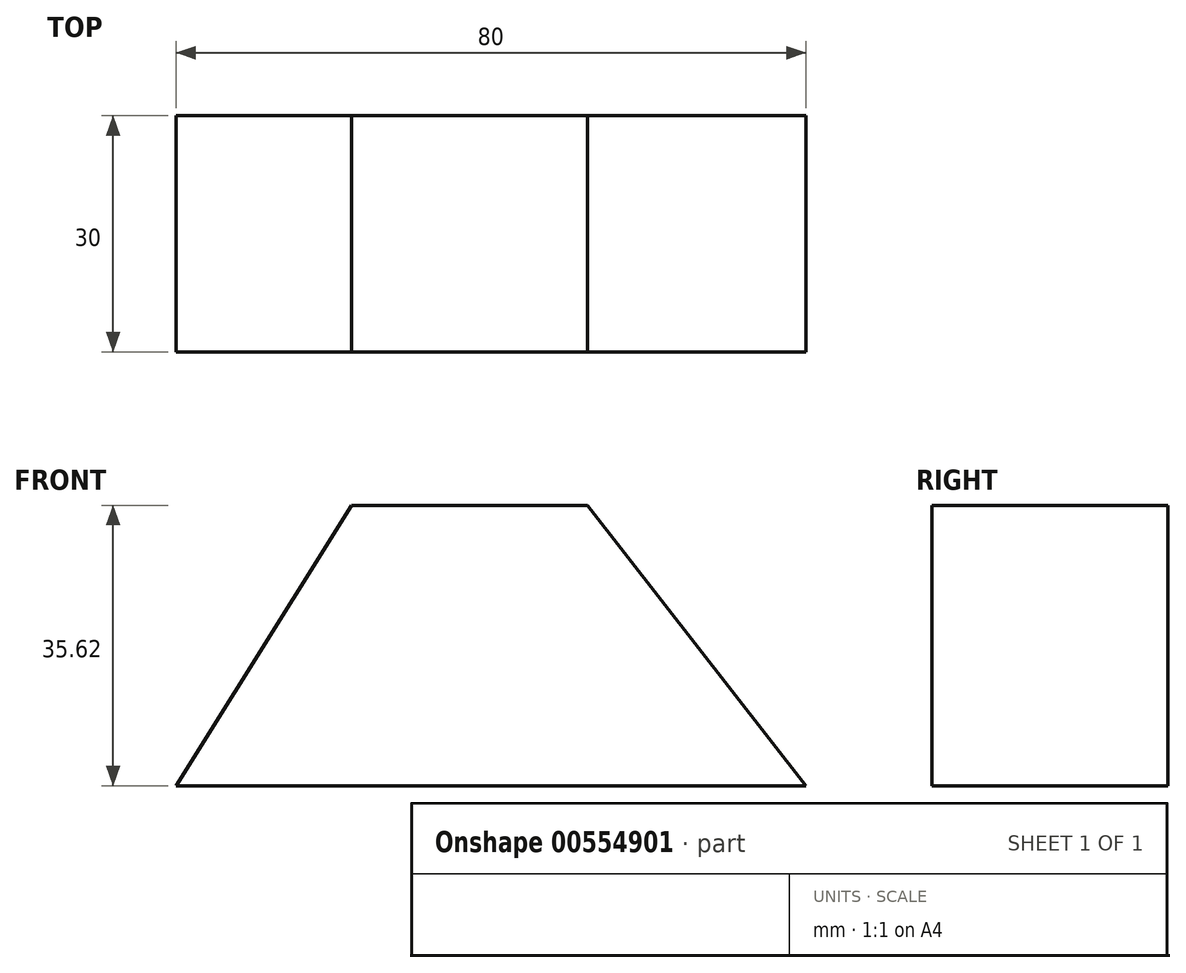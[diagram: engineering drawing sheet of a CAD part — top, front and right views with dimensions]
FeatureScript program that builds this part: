
annotation { "Feature Type Name" : "Feature", "Feature Type Description" : "" }
export const myFeature = defineFeature(function(context is Context, id is Id, definition is map)
    precondition{}
    {
        {
            var Q0;
            Q0=qCreatedBy(makeId("Front.planeOp"),FACE);
            var sketch = newSketch(context, id + "F0", { "sketchPlane" : qUnion([Q0])});
            skLineSegment(sketch, "E0", {"start": v(-80.96, 18.97) * mm, "end": v(-50.96, 18.97) * mm});
            skLineSegment(sketch, "E1", {"start": v(-50.96, 18.97) * mm, "end": v(-23.22, -16.65) * mm});
            skLineSegment(sketch, "E2", {"start": v(-23.22, -16.65) * mm, "end": v(-103.22, -16.65) * mm});
            skLineSegment(sketch, "E3", {"start": v(-103.22, -16.65) * mm, "end": v(-80.96, 18.97) * mm});
            skSolve(sketch);
        }
        {
            var Q0;
            Q0 = qSketchRegion(id + "F0", true);
            extrude(context, id + "F1", {"entities" : qUnion([Q0]), "depth" : 30 * mm, "offsetDistance" : 25 * mm});
        }
    });
